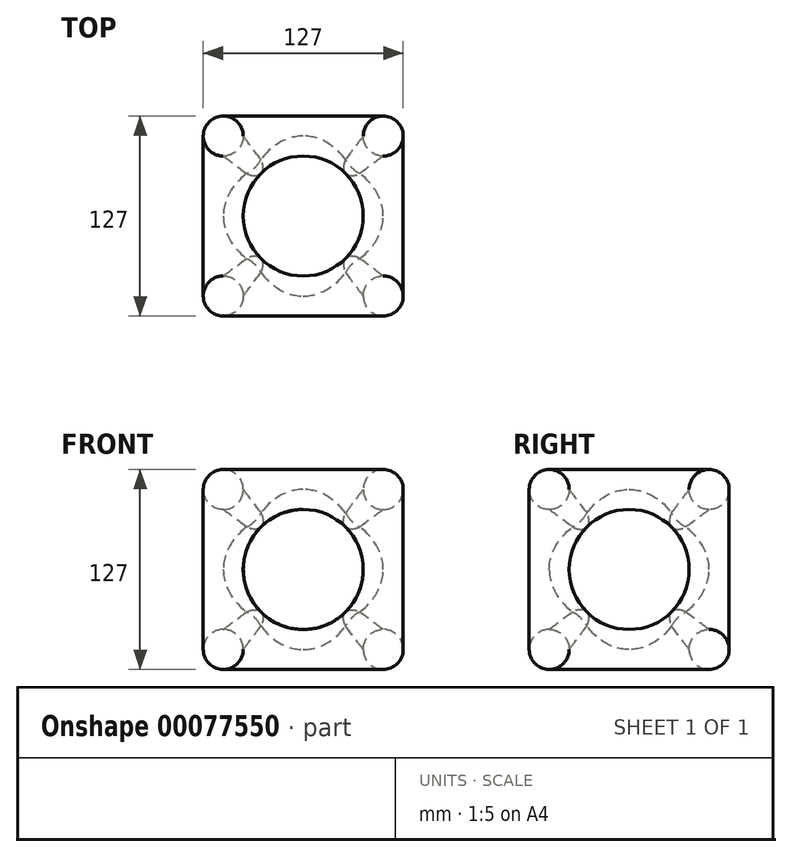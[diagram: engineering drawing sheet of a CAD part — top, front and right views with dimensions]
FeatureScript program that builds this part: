
annotation { "Feature Type Name" : "Feature", "Feature Type Description" : "" }
export const myFeature = defineFeature(function(context is Context, id is Id, definition is map)
    precondition{}
    {
        {
            var Q0;
            Q0=qCreatedBy(makeId("Top.planeOp"),FACE);
            var sketch = newSketch(context, id + "F0", { "sketchPlane" : qUnion([Q0])});
            skLineSegment(sketch, "E0.bottom", {"start": v(-64.54, 63.56) * mm, "end": v(62.46, 63.56) * mm});
            skLineSegment(sketch, "E0.top", {"start": v(-64.54, -63.44) * mm, "end": v(62.46, -63.44) * mm});
            skLineSegment(sketch, "E0.left", {"start": v(-64.54, 63.56) * mm, "end": v(-64.54, -63.44) * mm});
            skLineSegment(sketch, "E0.right", {"start": v(62.46, 63.56) * mm, "end": v(62.46, -63.44) * mm});
            skSolve(sketch);
        }
        {
            var Q0;
            Q0=makeQuery(id+"F0.imprint","IMPRINT",FACE,{"disambiguationData":[TD([[makeQuery(id+"F0.imprint","IMPRINT",EDGE,{"derivedFrom":sQuery(id+"F0.wireOp",EDGE,"E0.bottom")}),-1.0]])]});
            extrude(context, id + "F1", {"entities" : qUnion([Q0]), "depth" : 127 * mm});
        }
        {
            var Q0;
            Q0=makeQuery(id+"F1.opExtrude","SWEPT_FACE",FACE,{"disambiguationData":[OSD([sQuery(id+"F0.wireOp",EDGE,"E0.bottom")])]});
            var sketch = newSketch(context, id + "F2", { "sketchPlane" : qUnion([Q0])});
            skCircle(sketch, "E1", {"center": v(1.04, 63.5) * mm, "radius": 38.1 * mm});
            skSolve(sketch);
        }
        {
            var Q0;
            Q0=makeQuery(id+"F2.imprint","IMPRINT",FACE,{"disambiguationData":[TD([[makeQuery(id+"F2.imprint","IMPRINT",EDGE,{"derivedFrom":sQuery(id+"F2.wireOp",EDGE,"E1")}),1.0]])]});
            extrude(context, id + "F3", {"entities" : qUnion([Q0]), "operationType" : NewBodyOperationType.REMOVE, "oppositeDirection" : true, "depth" : 127 * mm});
        }
        {
            var Q0;
            Q0=makeQuery(id+"F1.opExtrude","SWEPT_FACE",FACE,{"disambiguationData":[OSD([sQuery(id+"F0.wireOp",EDGE,"E0.right")])]});
            var sketch = newSketch(context, id + "F4", { "sketchPlane" : qUnion([Q0])});
            skCircle(sketch, "E2", {"center": v(0.06, 63.5) * mm, "radius": 38.1 * mm});
            skSolve(sketch);
        }
        {
            var Q0;
            Q0=makeQuery(id+"F4.imprint","IMPRINT",FACE,{"disambiguationData":[TD([[makeQuery(id+"F4.imprint","IMPRINT",EDGE,{"derivedFrom":sQuery(id+"F4.wireOp",EDGE,"E2")}),1.0]])]});
            extrude(context, id + "F5", {"entities" : qUnion([Q0]), "operationType" : NewBodyOperationType.REMOVE, "oppositeDirection" : true, "depth" : 127 * mm});
        }
        {
            var Q0;
            Q0=makeQuery(id+"F1.opExtrude","CAP_FACE",FACE,{"disambiguationData":[OSD([sQuery(id+"F0.wireOp",EDGE,"E0.bottom"),sQuery(id+"F0.wireOp",EDGE,"E0.top"),sQuery(id+"F0.wireOp",EDGE,"E0.left"),sQuery(id+"F0.wireOp",EDGE,"E0.right")])],"isStart":false});
            var sketch = newSketch(context, id + "F6", { "sketchPlane" : qUnion([Q0])});
            skCircle(sketch, "E3", {"center": v(-1.04, 0.06) * mm, "radius": 38.1 * mm});
            skSolve(sketch);
        }
        {
            var Q0;
            Q0=makeQuery(id+"F6.imprint","IMPRINT",FACE,{"disambiguationData":[TD([[makeQuery(id+"F6.imprint","IMPRINT",EDGE,{"derivedFrom":sQuery(id+"F6.wireOp",EDGE,"E3")}),1.0]])]});
            extrude(context, id + "F7", {"entities" : qUnion([Q0]), "operationType" : NewBodyOperationType.REMOVE, "oppositeDirection" : true, "depth" : 127 * mm});
        }
        {
            var Q0;
            Q0=makeQuery(id+"F3.boolean.opBoolean","COPY",EDGE,{"derivedFrom":makeQuery(id+"F3.opExtrude","CAP_EDGE",EDGE,{"disambiguationData":[OSD([sQuery(id+"F2.wireOp",EDGE,"E1")])],"isStart":true})});
            var Q1;
            Q1=makeQuery(id+"F7.boolean.opBoolean","COPY",EDGE,{"derivedFrom":makeQuery(id+"F7.opExtrude","CAP_EDGE",EDGE,{"disambiguationData":[OSD([sQuery(id+"F6.wireOp",EDGE,"E3")])],"isStart":false})});
            var Q2;
            Q2=makeQuery(id+"F1.opExtrude","SWEPT_EDGE",EDGE,{"disambiguationData":[OSD([sQuery(id+"F0.wireOp",EDGE,"E0.bottom"),sQuery(id+"F0.wireOp",EDGE,"E0.right")])]});
            var Q3;
            Q3=makeQuery(id+"F7.boolean.opBoolean","COPY",EDGE,{"derivedFrom":makeQuery(id+"F7.opExtrude","CAP_EDGE",EDGE,{"disambiguationData":[OSD([sQuery(id+"F6.wireOp",EDGE,"E3")])],"isStart":true})});
            var Q4;
            Q4=makeQuery(id+"F1.opExtrude","SWEPT_EDGE",EDGE,{"disambiguationData":[OSD([sQuery(id+"F0.wireOp",EDGE,"E0.top"),sQuery(id+"F0.wireOp",EDGE,"E0.left")])]});
            var Q5;
            Q5=makeQuery(id+"F5.boolean.opBoolean","INTERSECT",EDGE,{"disambiguationData":[OD(0.0)],"derivedFrom":[makeQuery(id+"F3.boolean.opBoolean","COPY",FACE,{"derivedFrom":makeQuery(id+"F3.opExtrude","SWEPT_FACE",FACE,{"disambiguationData":[OSD([sQuery(id+"F2.wireOp",EDGE,"E1")])]})}),makeQuery(id+"F5.opExtrude","SWEPT_FACE",FACE,{"disambiguationData":[OSD([sQuery(id+"F4.wireOp",EDGE,"E2")])]})]});
            var Q6;
            Q6=makeQuery(id+"F1.opExtrude","SWEPT_EDGE",EDGE,{"disambiguationData":[OSD([sQuery(id+"F0.wireOp",EDGE,"E0.top"),sQuery(id+"F0.wireOp",EDGE,"E0.right")])]});
            var Q7;
            Q7=makeQuery(id+"F5.boolean.opBoolean","COPY",EDGE,{"derivedFrom":makeQuery(id+"F5.opExtrude","CAP_EDGE",EDGE,{"disambiguationData":[OSD([sQuery(id+"F4.wireOp",EDGE,"E2")])],"isStart":false})});
            var Q8;
            Q8=makeQuery(id+"F1.opExtrude","SWEPT_FACE",FACE,{"disambiguationData":[OSD([sQuery(id+"F0.wireOp",EDGE,"E0.right")])]});
            var Q9;
            Q9=makeQuery(id+"F1.opExtrude","CAP_EDGE",EDGE,{"disambiguationData":[OSD([sQuery(id+"F0.wireOp",EDGE,"E0.bottom")])],"isStart":false});
            var Q10;
            Q10=makeQuery(id+"F1.opExtrude","CAP_EDGE",EDGE,{"disambiguationData":[OSD([sQuery(id+"F0.wireOp",EDGE,"E0.top")])],"isStart":true});
            var Q11;
            Q11=makeQuery(id+"F1.opExtrude","CAP_EDGE",EDGE,{"disambiguationData":[OSD([sQuery(id+"F0.wireOp",EDGE,"E0.top")])],"isStart":false});
            var Q12;
            Q12=makeQuery(id+"F1.opExtrude","CAP_EDGE",EDGE,{"disambiguationData":[OSD([sQuery(id+"F0.wireOp",EDGE,"E0.left")])],"isStart":false});
            var Q13;
            Q13=makeQuery(id+"F1.opExtrude","CAP_EDGE",EDGE,{"disambiguationData":[OSD([sQuery(id+"F0.wireOp",EDGE,"E0.right")])],"isStart":true});
            var Q14;
            Q14=makeQuery(id+"F1.opExtrude","CAP_EDGE",EDGE,{"disambiguationData":[OSD([sQuery(id+"F0.wireOp",EDGE,"E0.right")])],"isStart":false});
            var Q15;
            Q15=makeQuery(id+"F1.opExtrude","SWEPT_FACE",FACE,{"disambiguationData":[OSD([sQuery(id+"F0.wireOp",EDGE,"E0.bottom")])]});
            var Q16;
            Q16=makeQuery(id+"F3.boolean.opBoolean","COPY",EDGE,{"derivedFrom":makeQuery(id+"F3.opExtrude","CAP_EDGE",EDGE,{"disambiguationData":[OSD([sQuery(id+"F2.wireOp",EDGE,"E1")])],"isStart":false})});
            var Q17;
            Q17=makeQuery(id+"F1.opExtrude","SWEPT_FACE",FACE,{"disambiguationData":[OSD([sQuery(id+"F0.wireOp",EDGE,"E0.top")])]});
            var Q18;
            {var subQ0=makeQuery(id+"F3.boolean.opBoolean","COPY",FACE,{"derivedFrom":makeQuery(id+"F3.opExtrude","SWEPT_FACE",FACE,{"disambiguationData":[OSD([sQuery(id+"F2.wireOp",EDGE,"E1")])]})});Q18=makeQuery(id+"F5.boolean.opBoolean","SPLIT",FACE,{"disambiguationData":[TD([makeQuery(id+"F1.opExtrude","SWEPT_FACE",FACE,{"disambiguationData":[OSD([sQuery(id+"F0.wireOp",EDGE,"E0.bottom")])]})])],"derivedFrom":subQ0});}
            var Q19;
            {var subQ0=makeQuery(id+"F3.boolean.opBoolean","COPY",FACE,{"derivedFrom":makeQuery(id+"F3.opExtrude","SWEPT_FACE",FACE,{"disambiguationData":[OSD([sQuery(id+"F2.wireOp",EDGE,"E1")])]})});Q19=makeQuery(id+"F5.boolean.opBoolean","SPLIT",FACE,{"disambiguationData":[TD([makeQuery(id+"F1.opExtrude","SWEPT_FACE",FACE,{"disambiguationData":[OSD([sQuery(id+"F0.wireOp",EDGE,"E0.top")])]})])],"derivedFrom":subQ0});}
            var Q20;
            Q20=makeQuery(id+"F1.opExtrude","CAP_FACE",FACE,{"disambiguationData":[OSD([sQuery(id+"F0.wireOp",EDGE,"E0.bottom"),sQuery(id+"F0.wireOp",EDGE,"E0.top"),sQuery(id+"F0.wireOp",EDGE,"E0.left"),sQuery(id+"F0.wireOp",EDGE,"E0.right")])],"isStart":false});
            var Q21;
            Q21=makeQuery(id+"F1.opExtrude","CAP_FACE",FACE,{"disambiguationData":[OSD([sQuery(id+"F0.wireOp",EDGE,"E0.bottom"),sQuery(id+"F0.wireOp",EDGE,"E0.top"),sQuery(id+"F0.wireOp",EDGE,"E0.left"),sQuery(id+"F0.wireOp",EDGE,"E0.right")])],"isStart":true});
            var Q22;
            Q22=makeQuery(id+"F1.opExtrude","SWEPT_FACE",FACE,{"disambiguationData":[OSD([sQuery(id+"F0.wireOp",EDGE,"E0.left")])]});
            var Q23;
            Q23=makeQuery(id+"F5.boolean.opBoolean","COPY",EDGE,{"derivedFrom":makeQuery(id+"F5.opExtrude","CAP_EDGE",EDGE,{"disambiguationData":[OSD([sQuery(id+"F4.wireOp",EDGE,"E2")])],"isStart":true})});
            var Q24;
            Q24=makeQuery(id+"F5.boolean.opBoolean","INTERSECT",EDGE,{"disambiguationData":[OD(1.0)],"derivedFrom":[makeQuery(id+"F3.boolean.opBoolean","COPY",FACE,{"derivedFrom":makeQuery(id+"F3.opExtrude","SWEPT_FACE",FACE,{"disambiguationData":[OSD([sQuery(id+"F2.wireOp",EDGE,"E1")])]})}),makeQuery(id+"F5.opExtrude","SWEPT_FACE",FACE,{"disambiguationData":[OSD([sQuery(id+"F4.wireOp",EDGE,"E2")])]})]});
            var Q25;
            Q25=makeQuery(id+"F5.boolean.opBoolean","COPY",FACE,{"disambiguationData":[OD(0.0)],"derivedFrom":makeQuery(id+"F5.opExtrude","SWEPT_FACE",FACE,{"disambiguationData":[OSD([sQuery(id+"F4.wireOp",EDGE,"E2")])]})});
            var Q26;
            Q26=makeQuery(id+"F5.boolean.opBoolean","COPY",FACE,{"disambiguationData":[OD(1.0)],"derivedFrom":makeQuery(id+"F5.opExtrude","SWEPT_FACE",FACE,{"disambiguationData":[OSD([sQuery(id+"F4.wireOp",EDGE,"E2")])]})});
            var Q27;
            Q27=makeQuery(id+"F5.boolean.opBoolean","INTERSECT",EDGE,{"disambiguationData":[OD(3.0)],"derivedFrom":[makeQuery(id+"F3.boolean.opBoolean","COPY",FACE,{"derivedFrom":makeQuery(id+"F3.opExtrude","SWEPT_FACE",FACE,{"disambiguationData":[OSD([sQuery(id+"F2.wireOp",EDGE,"E1")])]})}),makeQuery(id+"F5.opExtrude","SWEPT_FACE",FACE,{"disambiguationData":[OSD([sQuery(id+"F4.wireOp",EDGE,"E2")])]})]});
            var Q28;
            {var subQ0=makeQuery(id+"F3.boolean.opBoolean","COPY",FACE,{"derivedFrom":makeQuery(id+"F3.opExtrude","SWEPT_FACE",FACE,{"disambiguationData":[OSD([sQuery(id+"F2.wireOp",EDGE,"E1")])]})});Q28=makeQuery(id+"F7.boolean.opBoolean","INTERSECT",EDGE,{"disambiguationData":[OD(0.0)],"derivedFrom":[makeQuery(id+"F5.boolean.opBoolean","SPLIT",FACE,{"disambiguationData":[TD([makeQuery(id+"F1.opExtrude","SWEPT_FACE",FACE,{"disambiguationData":[OSD([sQuery(id+"F0.wireOp",EDGE,"E0.bottom")])]})])],"derivedFrom":subQ0}),makeQuery(id+"F7.opExtrude","SWEPT_FACE",FACE,{"disambiguationData":[OSD([sQuery(id+"F6.wireOp",EDGE,"E3")])]})]});}
            var Q29;
            Q29=makeQuery(id+"F7.boolean.opBoolean","COPY",FACE,{"disambiguationData":[OD(0.0)],"derivedFrom":makeQuery(id+"F7.opExtrude","SWEPT_FACE",FACE,{"disambiguationData":[OSD([sQuery(id+"F6.wireOp",EDGE,"E3")])]})});
            var Q30;
            Q30=makeQuery(id+"F7.boolean.opBoolean","COPY",FACE,{"disambiguationData":[OD(1.0)],"derivedFrom":makeQuery(id+"F7.opExtrude","SWEPT_FACE",FACE,{"disambiguationData":[OSD([sQuery(id+"F6.wireOp",EDGE,"E3")])]})});
            var Q31;
            {var subQ0=makeQuery(id+"F3.boolean.opBoolean","COPY",FACE,{"derivedFrom":makeQuery(id+"F3.opExtrude","SWEPT_FACE",FACE,{"disambiguationData":[OSD([sQuery(id+"F2.wireOp",EDGE,"E1")])]})});Q31=makeQuery(id+"F7.boolean.opBoolean","INTERSECT",EDGE,{"disambiguationData":[OD(1.0)],"derivedFrom":[makeQuery(id+"F5.boolean.opBoolean","SPLIT",FACE,{"disambiguationData":[TD([makeQuery(id+"F1.opExtrude","SWEPT_FACE",FACE,{"disambiguationData":[OSD([sQuery(id+"F0.wireOp",EDGE,"E0.top")])]})])],"derivedFrom":subQ0}),makeQuery(id+"F7.opExtrude","SWEPT_FACE",FACE,{"disambiguationData":[OSD([sQuery(id+"F6.wireOp",EDGE,"E3")])]})]});}
            var Q32;
            Q32=makeQuery(id+"F7.boolean.opBoolean","INTERSECT",EDGE,{"disambiguationData":[OD(1.0)],"derivedFrom":[makeQuery(id+"F5.boolean.opBoolean","COPY",FACE,{"disambiguationData":[OD(0.0)],"derivedFrom":makeQuery(id+"F5.opExtrude","SWEPT_FACE",FACE,{"disambiguationData":[OSD([sQuery(id+"F4.wireOp",EDGE,"E2")])]})}),makeQuery(id+"F7.opExtrude","SWEPT_FACE",FACE,{"disambiguationData":[OSD([sQuery(id+"F6.wireOp",EDGE,"E3")])]})]});
            var Q33;
            Q33=makeQuery(id+"F7.boolean.opBoolean","INTERSECT",EDGE,{"disambiguationData":[OD(0.0)],"derivedFrom":[makeQuery(id+"F5.boolean.opBoolean","COPY",FACE,{"disambiguationData":[OD(1.0)],"derivedFrom":makeQuery(id+"F5.opExtrude","SWEPT_FACE",FACE,{"disambiguationData":[OSD([sQuery(id+"F4.wireOp",EDGE,"E2")])]})}),makeQuery(id+"F7.opExtrude","SWEPT_FACE",FACE,{"disambiguationData":[OSD([sQuery(id+"F6.wireOp",EDGE,"E3")])]})]});
            var Q34;
            Q34=makeQuery(id+"F1.opExtrude","SWEPT_EDGE",EDGE,{"disambiguationData":[OSD([sQuery(id+"F0.wireOp",EDGE,"E0.bottom"),sQuery(id+"F0.wireOp",EDGE,"E0.left")])]});
            var Q35;
            Q35=makeQuery(id+"F1.opExtrude","CAP_EDGE",EDGE,{"disambiguationData":[OSD([sQuery(id+"F0.wireOp",EDGE,"E0.bottom")])],"isStart":true});
            var Q36;
            Q36=makeQuery(id+"F1.opExtrude","CAP_EDGE",EDGE,{"disambiguationData":[OSD([sQuery(id+"F0.wireOp",EDGE,"E0.left")])],"isStart":true});
            var Q37;
            Q37=makeQuery(id+"F7.boolean.opBoolean","INTERSECT",EDGE,{"disambiguationData":[OD(1.0)],"derivedFrom":[makeQuery(id+"F5.boolean.opBoolean","COPY",FACE,{"disambiguationData":[OD(1.0)],"derivedFrom":makeQuery(id+"F5.opExtrude","SWEPT_FACE",FACE,{"disambiguationData":[OSD([sQuery(id+"F4.wireOp",EDGE,"E2")])]})}),makeQuery(id+"F7.opExtrude","SWEPT_FACE",FACE,{"disambiguationData":[OSD([sQuery(id+"F6.wireOp",EDGE,"E3")])]})]});
            var Q38;
            Q38=makeQuery(id+"F5.boolean.opBoolean","INTERSECT",EDGE,{"disambiguationData":[OD(2.0)],"derivedFrom":[makeQuery(id+"F3.boolean.opBoolean","COPY",FACE,{"derivedFrom":makeQuery(id+"F3.opExtrude","SWEPT_FACE",FACE,{"disambiguationData":[OSD([sQuery(id+"F2.wireOp",EDGE,"E1")])]})}),makeQuery(id+"F5.opExtrude","SWEPT_FACE",FACE,{"disambiguationData":[OSD([sQuery(id+"F4.wireOp",EDGE,"E2")])]})]});
            var Q39;
            {var subQ0=makeQuery(id+"F3.boolean.opBoolean","COPY",FACE,{"derivedFrom":makeQuery(id+"F3.opExtrude","SWEPT_FACE",FACE,{"disambiguationData":[OSD([sQuery(id+"F2.wireOp",EDGE,"E1")])]})});Q39=makeQuery(id+"F7.boolean.opBoolean","INTERSECT",EDGE,{"disambiguationData":[OD(1.0)],"derivedFrom":[makeQuery(id+"F5.boolean.opBoolean","SPLIT",FACE,{"disambiguationData":[TD([makeQuery(id+"F1.opExtrude","SWEPT_FACE",FACE,{"disambiguationData":[OSD([sQuery(id+"F0.wireOp",EDGE,"E0.bottom")])]})])],"derivedFrom":subQ0}),makeQuery(id+"F7.opExtrude","SWEPT_FACE",FACE,{"disambiguationData":[OSD([sQuery(id+"F6.wireOp",EDGE,"E3")])]})]});}
            var Q40;
            {var subQ0=makeQuery(id+"F3.boolean.opBoolean","COPY",FACE,{"derivedFrom":makeQuery(id+"F3.opExtrude","SWEPT_FACE",FACE,{"disambiguationData":[OSD([sQuery(id+"F2.wireOp",EDGE,"E1")])]})});Q40=makeQuery(id+"F7.boolean.opBoolean","INTERSECT",EDGE,{"disambiguationData":[OD(0.0)],"derivedFrom":[makeQuery(id+"F5.boolean.opBoolean","SPLIT",FACE,{"disambiguationData":[TD([makeQuery(id+"F1.opExtrude","SWEPT_FACE",FACE,{"disambiguationData":[OSD([sQuery(id+"F0.wireOp",EDGE,"E0.top")])]})])],"derivedFrom":subQ0}),makeQuery(id+"F7.opExtrude","SWEPT_FACE",FACE,{"disambiguationData":[OSD([sQuery(id+"F6.wireOp",EDGE,"E3")])]})]});}
            var Q41;
            Q41=makeQuery(id+"F7.boolean.opBoolean","INTERSECT",EDGE,{"disambiguationData":[OD(0.0)],"derivedFrom":[makeQuery(id+"F5.boolean.opBoolean","COPY",FACE,{"disambiguationData":[OD(0.0)],"derivedFrom":makeQuery(id+"F5.opExtrude","SWEPT_FACE",FACE,{"disambiguationData":[OSD([sQuery(id+"F4.wireOp",EDGE,"E2")])]})}),makeQuery(id+"F7.opExtrude","SWEPT_FACE",FACE,{"disambiguationData":[OSD([sQuery(id+"F6.wireOp",EDGE,"E3")])]})]});
            fillet(context, id + "F8", {"entities" : qUnion([Q0, Q1, Q2, Q3, Q4, Q5, Q6, Q7, Q8, Q9, Q10, Q11, Q12, Q13, Q14, Q15, Q16, Q17, Q18, Q19, Q20, Q21, Q22, Q23, Q24, Q25, Q26, Q27, Q28, Q29, Q30, Q31, Q32, Q33, Q34, Q35, Q36, Q37, Q38, Q39, Q40, Q41]), "radius" : 12.7 * mm, "tangentPropagation" : true, "allowEdgeOverflow" : false});
        }
    });
